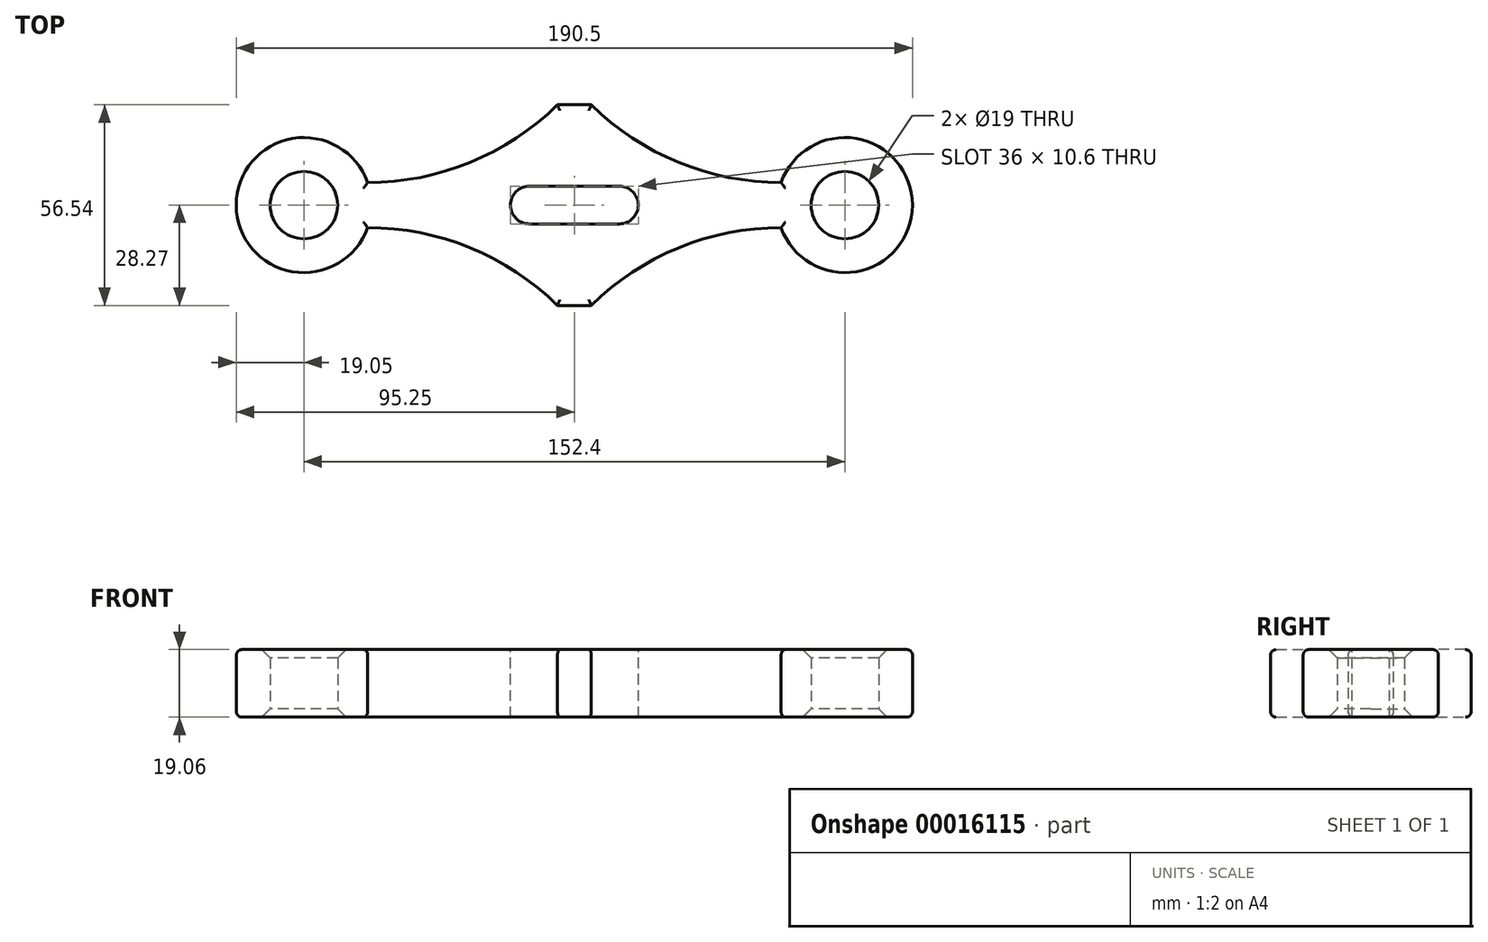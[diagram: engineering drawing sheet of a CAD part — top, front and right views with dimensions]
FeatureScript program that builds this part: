
annotation { "Feature Type Name" : "Feature", "Feature Type Description" : "" }
export const myFeature = defineFeature(function(context is Context, id is Id, definition is map)
    precondition{}
    {
        {
            var Q0;
            Q0=qCreatedBy(makeId("Top.planeOp"),FACE);
            var sketch = newSketch(context, id + "F0", { "sketchPlane" : qUnion([Q0])});
            skArc(sketch, "E0", {"start": v(95.25, 0) * mm, "mid": v(79.42, 18.78) * mm, "end": v(58.24, 6.35) * mm});
            skArc(sketch, "E1", {"start": v(4.76, 28.27) * mm, "mid": v(29.34, 12.04) * mm, "end": v(58.24, 6.35) * mm});
            skArc(sketch, "E2", {"start": v(85.7, 0) * mm, "mid": v(76.2, 9.5) * mm, "end": v(66.7, 0) * mm});
            skLineSegment(sketch, "E3", {"start": v(0, 0) * mm, "end": v(66.7, 0) * mm});
            skLineSegment(sketch, "E4", {"start": v(0, 28.27) * mm, "end": v(0, 0) * mm});
            skLineSegment(sketch, "E5.trimOffspring", {"start": v(85.7, 0) * mm, "end": v(95.25, 0) * mm});
            skLineSegment(sketch, "E6", {"start": v(0, 28.27) * mm, "end": v(4.76, 28.27) * mm});
            skPoint(sketch, "E7.orphan", {"position": v(0, 33.41) * mm});
            skSolve(sketch);
        }
        {
            var Q0;
            Q0=makeQuery(id+"F0.imprint","IMPRINT",FACE,{"disambiguationData":[TD([[makeQuery(id+"F0.imprint","IMPRINT",EDGE,{"derivedFrom":sQuery(id+"F0.wireOp",EDGE,"E0")}),1.0]])]});
            extrude(context, id + "F1", {"entities" : qUnion([Q0]), "endBound" : BoundingType.SYMMETRIC, "depth" : 19.05 * mm});
        }
        {
            var Q0;
            Q0=makeQuery(id+"F1.opExtrude","SWEPT_BODY",BODY,{"disambiguationData":[OSD([sQuery(id+"F0.wireOp",EDGE,"E0"),sQuery(id+"F0.wireOp",EDGE,"E1"),sQuery(id+"F0.wireOp",EDGE,"E2"),sQuery(id+"F0.wireOp",EDGE,"E3"),sQuery(id+"F0.wireOp",EDGE,"E4"),sQuery(id+"F0.wireOp",EDGE,"E5.trimOffspring"),sQuery(id+"F0.wireOp",EDGE,"E6")])]});
            var Q1;
            Q1=qCreatedBy(makeId("Right.planeOp"),FACE);
            mirror(context, id + "F2", {"operationType" : NewBodyOperationType.ADD, "entities" : qUnion([Q0]), "mirrorPlane" : qUnion([Q1])});
        }
        {
            var Q0;
            Q0=makeQuery(id+"F1.opExtrude","SWEPT_BODY",BODY,{"disambiguationData":[OSD([sQuery(id+"F0.wireOp",EDGE,"E0"),sQuery(id+"F0.wireOp",EDGE,"E1"),sQuery(id+"F0.wireOp",EDGE,"E2"),sQuery(id+"F0.wireOp",EDGE,"E3"),sQuery(id+"F0.wireOp",EDGE,"E4"),sQuery(id+"F0.wireOp",EDGE,"E5.trimOffspring"),sQuery(id+"F0.wireOp",EDGE,"E6")])]});
            var Q1;
            Q1=qCreatedBy(makeId("Front.planeOp"),FACE);
            mirror(context, id + "F3", {"operationType" : NewBodyOperationType.ADD, "entities" : qUnion([Q0]), "mirrorPlane" : qUnion([Q1])});
        }
        {
            var Q0;
            {var subQ0=makeQuery(id+"F2.opPattern","COPY",FACE,{"derivedFrom":makeQuery(id+"F1.opExtrude","SWEPT_FACE",FACE,{"disambiguationData":[OSD([sQuery(id+"F0.wireOp",EDGE,"E2")])]}),"instanceName":"1"});Q0=makeQuery(id+"F3.boolean.opBoolean","MERGE",FACE,{"derivedFrom":[subQ0,makeQuery(id+"F3.opPattern","COPY",FACE,{"derivedFrom":subQ0,"instanceName":"1"})]});}
            var Q1;
            {var subQ0=makeQuery(id+"F1.opExtrude","SWEPT_FACE",FACE,{"disambiguationData":[OSD([sQuery(id+"F0.wireOp",EDGE,"E2")])]});Q1=makeQuery(id+"F3.boolean.opBoolean","MERGE",FACE,{"derivedFrom":[subQ0,makeQuery(id+"F3.opPattern","COPY",FACE,{"derivedFrom":subQ0,"instanceName":"1"})]});}
            chamfer(context, id + "F4", {"entities" : qUnion([Q0, Q1]), "width" : 2.38 * mm, "tangentPropagation" : true});
        }
        {
            var Q0;
            {var subQ0=makeQuery(id+"F1.opExtrude","CAP_FACE",FACE,{"disambiguationData":[OSD([sQuery(id+"F0.wireOp",EDGE,"E0"),sQuery(id+"F0.wireOp",EDGE,"E1"),sQuery(id+"F0.wireOp",EDGE,"E2"),sQuery(id+"F0.wireOp",EDGE,"E3"),sQuery(id+"F0.wireOp",EDGE,"E4"),sQuery(id+"F0.wireOp",EDGE,"E5.trimOffspring"),sQuery(id+"F0.wireOp",EDGE,"E6")])],"isStart":false});var subQ1=makeQuery(id+"F2.boolean.opBoolean","MERGE",FACE,{"derivedFrom":[subQ0,makeQuery(id+"F2.opPattern","COPY",FACE,{"derivedFrom":subQ0,"instanceName":"1"})]});Q0=makeQuery(id+"F3.boolean.opBoolean","MERGE",FACE,{"derivedFrom":[subQ1,makeQuery(id+"F3.opPattern","COPY",FACE,{"derivedFrom":subQ1,"instanceName":"1"})]});}
            var Q1;
            {var subQ0=makeQuery(id+"F1.opExtrude","CAP_FACE",FACE,{"disambiguationData":[OSD([sQuery(id+"F0.wireOp",EDGE,"E0"),sQuery(id+"F0.wireOp",EDGE,"E1"),sQuery(id+"F0.wireOp",EDGE,"E2"),sQuery(id+"F0.wireOp",EDGE,"E3"),sQuery(id+"F0.wireOp",EDGE,"E4"),sQuery(id+"F0.wireOp",EDGE,"E5.trimOffspring"),sQuery(id+"F0.wireOp",EDGE,"E6")])],"isStart":true});var subQ1=makeQuery(id+"F2.boolean.opBoolean","MERGE",FACE,{"derivedFrom":[subQ0,makeQuery(id+"F2.opPattern","COPY",FACE,{"derivedFrom":subQ0,"instanceName":"1"})]});Q1=makeQuery(id+"F3.boolean.opBoolean","MERGE",FACE,{"derivedFrom":[subQ1,makeQuery(id+"F3.opPattern","COPY",FACE,{"derivedFrom":subQ1,"instanceName":"1"})]});}
            fillet(context, id + "F5", {"entities" : qUnion([Q0, Q1]), "radius" : 1.59 * mm, "tangentPropagation" : true, "allowEdgeOverflow" : false});
        }
        {
            var Q0;
            {var subQ0=makeQuery(id+"F1.opExtrude","CAP_FACE",FACE,{"disambiguationData":[OSD([sQuery(id+"F0.wireOp",EDGE,"E0"),sQuery(id+"F0.wireOp",EDGE,"E1"),sQuery(id+"F0.wireOp",EDGE,"E2"),sQuery(id+"F0.wireOp",EDGE,"E3"),sQuery(id+"F0.wireOp",EDGE,"E4"),sQuery(id+"F0.wireOp",EDGE,"E5.trimOffspring"),sQuery(id+"F0.wireOp",EDGE,"E6")])],"isStart":false});var subQ1=makeQuery(id+"F2.boolean.opBoolean","MERGE",FACE,{"derivedFrom":[subQ0,makeQuery(id+"F2.opPattern","COPY",FACE,{"derivedFrom":subQ0,"instanceName":"1"})]});Q0=makeQuery(id+"F3.boolean.opBoolean","MERGE",FACE,{"derivedFrom":[subQ1,makeQuery(id+"F3.opPattern","COPY",FACE,{"derivedFrom":subQ1,"instanceName":"1"})]});}
            var sketch = newSketch(context, id + "F6", { "sketchPlane" : qUnion([Q0])});
            skArc(sketch, "E8", {"start": v(12.7, -5.3) * mm, "mid": v(18, 0) * mm, "end": v(12.7, 5.3) * mm});
            skArc(sketch, "E9", {"start": v(-12.7, 5.3) * mm, "mid": v(-18, 0) * mm, "end": v(-12.7, -5.3) * mm});
            skLineSegment(sketch, "E10", {"start": v(-12.7, 5.3) * mm, "end": v(12.7, 5.3) * mm});
            skLineSegment(sketch, "E11", {"start": v(12.7, -5.3) * mm, "end": v(-12.7, -5.3) * mm});
            skSolve(sketch);
        }
        {
            var Q0;
            Q0=makeQuery(id+"F6.imprint","IMPRINT",FACE,{"disambiguationData":[TD([[makeQuery(id+"F6.imprint","IMPRINT",EDGE,{"derivedFrom":sQuery(id+"F6.wireOp",EDGE,"E8")}),1.0]])]});
            extrude(context, id + "F7", {"entities" : qUnion([Q0]), "operationType" : NewBodyOperationType.REMOVE, "endBound" : BoundingType.THROUGH_ALL, "oppositeDirection" : true, "depth" : 3.17 * mm});
        }
    });
